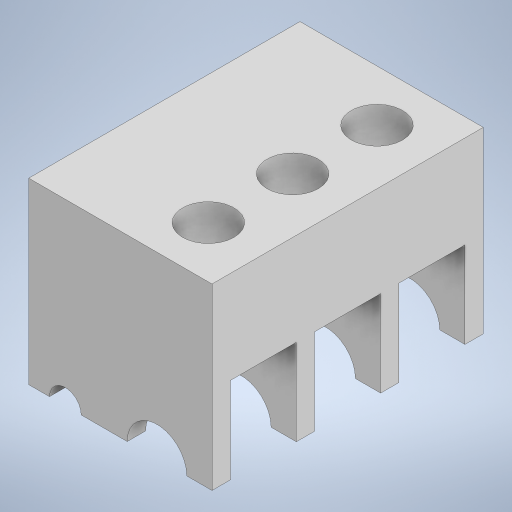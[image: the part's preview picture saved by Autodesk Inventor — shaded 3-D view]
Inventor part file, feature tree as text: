
AUTODESK INVENTOR PART (.ipt)
format: ipt  version: 2023 (Build 270158000, 158)  size: 282,624 bytes
history: native  units: in
note: dims shown in document units (in); Inventor stores cm internally (conversion verified against a paired STEP export)
features: extrude x4, sketch x3
ambient origin geometry x8: Origin, YZ Plane, XZ Plane, XY Plane, X Axis, Y Axis, Z Axis, Center Point
bodies: Solid1 (feature_tree)
feature tree (7):
  extrude  "Extrusion1"  Depth=4.878in
  sketch  "Sketch2"  dims[d2=1.625in d3=7.4in d4=0.0in]
  extrude  "Extrusion2"  Depth=7.4in TaperAngle=0.0deg
  extrude  "Extrusion3"  Depth=1.5in
  extrude  "Extrusion4"  Depth=1.5in
  sketch  "Sketch1"  dims[d0=5.0in d1=4.878in]
  sketch  "Sketch4"  dims[d6=1.4in d7=1.5in d10=1.4in d11=1.5in d13=2.3in d14=1.5in d15=1.4in d16=3.7in d17=6.0in d18=0.5in d20=2.528in d21=7.4in d22=0.0in d23=7.4in d24=0.0in d25=1.5in d26=0.866in d27=1.5in d28=0.0in d29=1.4in d30=0.0in d31=0.0in d32=0.0in]
